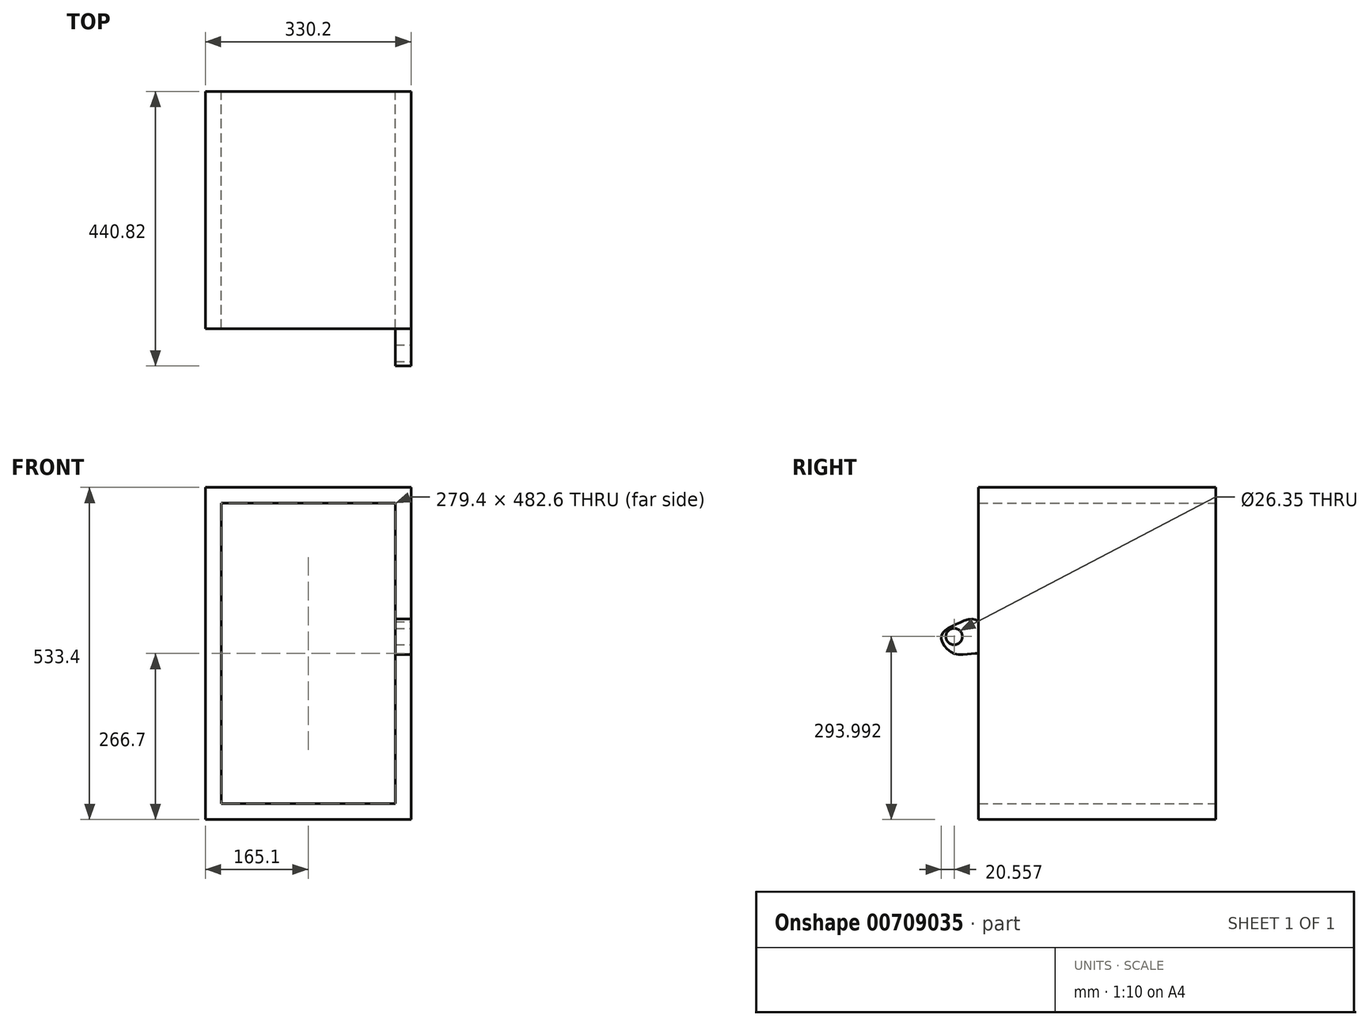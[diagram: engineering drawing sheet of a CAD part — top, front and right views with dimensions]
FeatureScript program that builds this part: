
annotation { "Feature Type Name" : "Feature", "Feature Type Description" : "" }
export const myFeature = defineFeature(function(context is Context, id is Id, definition is map)
    precondition{}
    {
        {
            var Q0;
            Q0=qCreatedBy(makeId("Front.planeOp"),FACE);
            var sketch = newSketch(context, id + "F0", { "sketchPlane" : qUnion([Q0])});
            skLineSegment(sketch, "E0.bottom", {"start": v(-57.96, 75.2) * mm, "end": v(57.96, 75.2) * mm});
            skLineSegment(sketch, "E0.top", {"start": v(-57.96, -75.2) * mm, "end": v(57.96, -75.2) * mm});
            skLineSegment(sketch, "E0.left", {"start": v(-57.96, 75.2) * mm, "end": v(-57.96, -75.2) * mm});
            skLineSegment(sketch, "E0.right", {"start": v(57.96, 75.2) * mm, "end": v(57.96, -75.2) * mm});
            skPoint(sketch, "E0.middle", {"position": v(0, 0) * mm});
            skLineSegment(sketch, "E1.bottom", {"start": v(-139.7, 241.3) * mm, "end": v(139.7, 241.3) * mm});
            skLineSegment(sketch, "E1.top", {"start": v(-139.7, -241.3) * mm, "end": v(139.7, -241.3) * mm});
            skLineSegment(sketch, "E1.left", {"start": v(-139.7, 241.3) * mm, "end": v(-139.7, -241.3) * mm});
            skLineSegment(sketch, "E1.right", {"start": v(139.7, 241.3) * mm, "end": v(139.7, -241.3) * mm});
            skLineSegment(sketch, "E2.bottom", {"start": v(-165.1, 266.7) * mm, "end": v(165.1, 266.7) * mm});
            skLineSegment(sketch, "E2.top", {"start": v(-165.1, -266.7) * mm, "end": v(165.1, -266.7) * mm});
            skLineSegment(sketch, "E2.left", {"start": v(-165.1, 266.7) * mm, "end": v(-165.1, -266.7) * mm});
            skLineSegment(sketch, "E2.right", {"start": v(165.1, 266.7) * mm, "end": v(165.1, -266.7) * mm});
            skSolve(sketch);
        }
        {
            var Q0;
            Q0=makeQuery(id+"F0.imprint","IMPRINT",FACE,{"disambiguationData":[TD([[makeQuery(id+"F0.imprint","IMPRINT",EDGE,{"derivedFrom":sQuery(id+"F0.wireOp",EDGE,"E1.bottom")}),1.0]])]});
            extrude(context, id + "F1", {"entities" : qUnion([Q0]), "depth" : 381 * mm, "offsetDistance" : 25.4 * mm});
        }
        {
            var Q0;
            Q0=makeQuery(id+"F1.opExtrude","SWEPT_FACE",FACE,{"disambiguationData":[OSD([sQuery(id+"F0.wireOp",EDGE,"E2.right")])]});
            var sketch = newSketch(context, id + "F2", { "sketchPlane" : qUnion([Q0])});
            skFitSpline(sketch, "E3", {"points": [v(-381, 0) * mm, v(-420.26, 0) * mm, v(-440.66, 27.69) * mm, v(-414.44, 48.08) * mm, v(-381, 51) * mm, v(-369.76, 0) * mm, v(-381, 0) * mm]});
            skCircle(sketch, "E4", {"center": v(-420.26, 27.3) * mm, "radius": 13.18 * mm});
            skSolve(sketch);
        }
        {
            var Q0;
            {var subQ0=sQuery(id+"F2.wireOp",EDGE,"E3");var subQ1=makeQuery(id+"F1.opExtrude","CAP_EDGE",EDGE,{"disambiguationData":[OSD([sQuery(id+"F0.wireOp",EDGE,"E2.right")])],"isStart":false});var subQ2=makeQuery(id+"F2.imprint","INTERSECT",VERTEX,{"disambiguationData":[OD(0.0)],"derivedFrom":[subQ1,subQ0]});Q0=makeQuery(id+"F2.imprint","IMPRINT",FACE,{"disambiguationData":[TD([[makeQuery(id+"F2.imprint","IMPRINT",EDGE,{"disambiguationData":[TD([[subQ2,1.0]])],"derivedFrom":subQ0}),-1.0]])]});}
            extrude(context, id + "F3", {"entities" : qUnion([Q0]), "oppositeDirection" : true, "depth" : 25.4 * mm, "offsetDistance" : 25.4 * mm});
        }
    });
